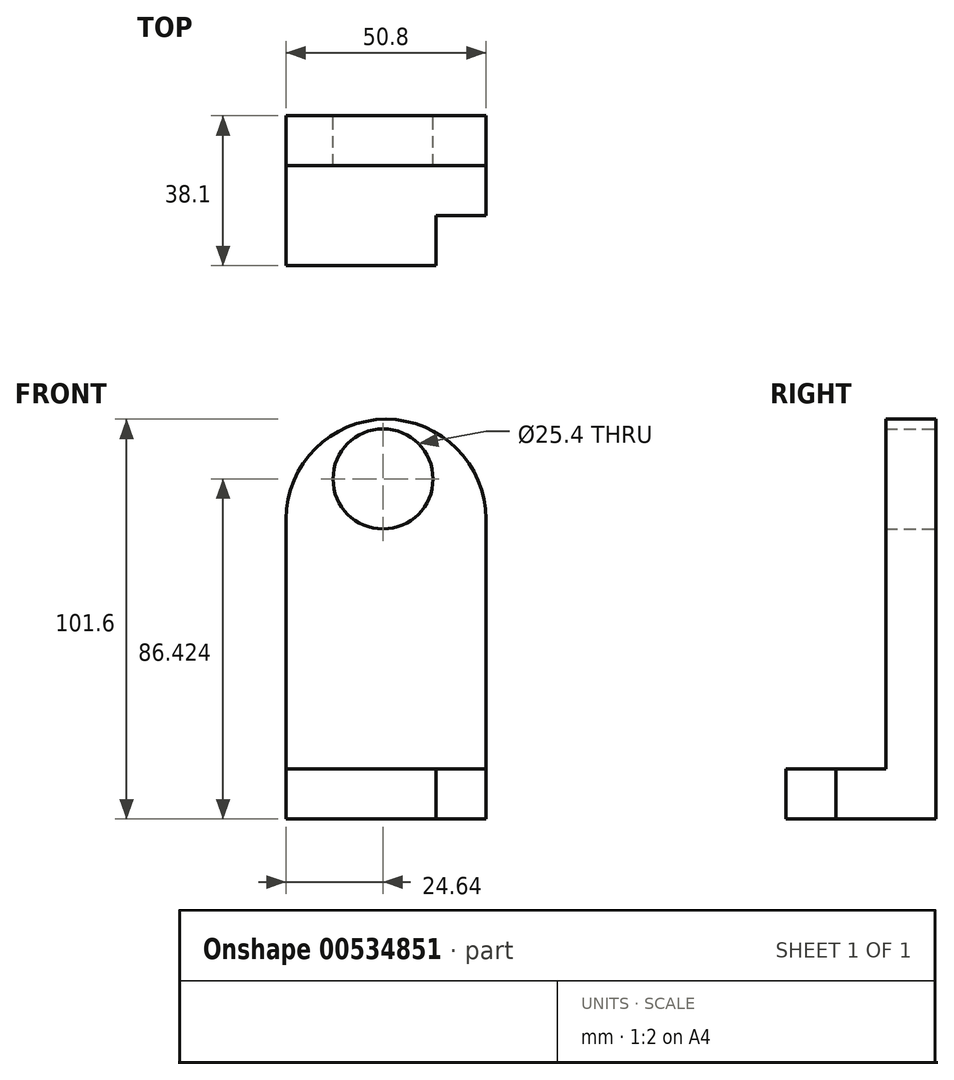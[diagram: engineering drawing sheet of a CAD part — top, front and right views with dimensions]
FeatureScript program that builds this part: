
annotation { "Feature Type Name" : "Feature", "Feature Type Description" : "" }
export const myFeature = defineFeature(function(context is Context, id is Id, definition is map)
    precondition{}
    {
        {
            var Q0;
            Q0=qCreatedBy(makeId("Front.planeOp"),FACE);
            var sketch = newSketch(context, id + "F0", { "sketchPlane" : qUnion([Q0])});
            skLineSegment(sketch, "E0.bottom", {"start": v(-24.64, 36.2) * mm, "end": v(26.16, 36.2) * mm});
            skLineSegment(sketch, "E0.top", {"start": v(-24.64, -40) * mm, "end": v(26.16, -40) * mm});
            skLineSegment(sketch, "E0.left", {"start": v(-24.64, 36.2) * mm, "end": v(-24.64, -40) * mm});
            skLineSegment(sketch, "E0.right", {"start": v(26.16, 36.2) * mm, "end": v(26.16, -40) * mm});
            skCircle(sketch, "E1", {"center": v(0.76, 36.2) * mm, "radius": 25.4 * mm});
            skPoint(sketch, "E1.third.point", {"position": v(12.9, 13.9) * mm});
            skSolve(sketch);
        }
        {
            var Q0;
            {var subQ0=sQuery(id+"F0.wireOp",EDGE,"E0.bottom");Q0=makeQuery(id+"F0.imprint","IMPRINT",FACE,{"disambiguationData":[TD([[makeQuery(id+"F0.imprint","IMPRINT",EDGE,{"derivedFrom":subQ0}),1.0]])]});}
            var Q1;
            Q1=makeQuery(id+"F0.imprint","IMPRINT",FACE,{"disambiguationData":[TD([[makeQuery(id+"F0.imprint","IMPRINT",EDGE,{"derivedFrom":sQuery(id+"F0.wireOp",EDGE,"E0.top")}),1.0]])]});
            var Q2;
            {var subQ0=sQuery(id+"F0.wireOp",EDGE,"E0.bottom");Q2=makeQuery(id+"F0.imprint","IMPRINT",FACE,{"disambiguationData":[TD([[makeQuery(id+"F0.imprint","IMPRINT",EDGE,{"derivedFrom":subQ0}),-1.0]])]});}
            extrude(context, id + "F1", {"entities" : qUnion([Q0, Q1, Q2]), "depth" : 12.7 * mm, "offsetDistance" : 25.4 * mm});
        }
        {
            var Q0;
            Q0=qCreatedBy(makeId("Front.planeOp"),FACE);
            var sketch = newSketch(context, id + "F2", { "sketchPlane" : qUnion([Q0])});
            skCircle(sketch, "E2", {"center": v(0, 46.42) * mm, "radius": 12.7 * mm});
            skSolve(sketch);
        }
        {
            var Q0;
            Q0 = qSketchRegion(id + "F2", true);
            extrude(context, id + "F3", {"entities" : qUnion([Q0]), "operationType" : NewBodyOperationType.REMOVE, "depth" : 12.7 * mm, "offsetDistance" : 25.4 * mm});
        }
        {
            var Q0;
            Q0=qCreatedBy(makeId("Front.planeOp"),FACE);
            var sketch = newSketch(context, id + "F4", { "sketchPlane" : qUnion([Q0])});
            skLineSegment(sketch, "E3.bottom", {"start": v(-24.64, -27.3) * mm, "end": v(26.16, -27.3) * mm});
            skLineSegment(sketch, "E3.top", {"start": v(-24.64, -40) * mm, "end": v(26.16, -40) * mm});
            skLineSegment(sketch, "E3.left", {"start": v(-24.64, -27.3) * mm, "end": v(-24.64, -40) * mm});
            skLineSegment(sketch, "E3.right", {"start": v(26.16, -27.3) * mm, "end": v(26.16, -40) * mm});
            skSolve(sketch);
        }
        {
            var Q0;
            Q0 = qSketchRegion(id + "F4", true);
            extrude(context, id + "F5", {"entities" : qUnion([Q0]), "operationType" : NewBodyOperationType.ADD, "depth" : 38.1 * mm, "offsetDistance" : 25.4 * mm});
        }
        {
            var Q0;
            Q0=qCreatedBy(makeId("Top.planeOp"),FACE);
            var sketch = newSketch(context, id + "F6", { "sketchPlane" : qUnion([Q0])});
            skLineSegment(sketch, "E4.bottom", {"start": v(26.16, -25.4) * mm, "end": v(13.46, -25.4) * mm});
            skLineSegment(sketch, "E4.top", {"start": v(26.16, -38.1) * mm, "end": v(13.46, -38.1) * mm});
            skLineSegment(sketch, "E4.left", {"start": v(26.16, -25.4) * mm, "end": v(26.16, -38.1) * mm});
            skLineSegment(sketch, "E4.right", {"start": v(13.46, -25.4) * mm, "end": v(13.46, -38.1) * mm});
            skSolve(sketch);
        }
        {
            var Q0;
            Q0 = qSketchRegion(id + "F6", true);
            extrude(context, id + "F7", {"entities" : qUnion([Q0]), "operationType" : NewBodyOperationType.REMOVE, "endBound" : BoundingType.THROUGH_ALL, "oppositeDirection" : true, "depth" : 25.4 * mm, "offsetDistance" : 25.4 * mm});
        }
    });
